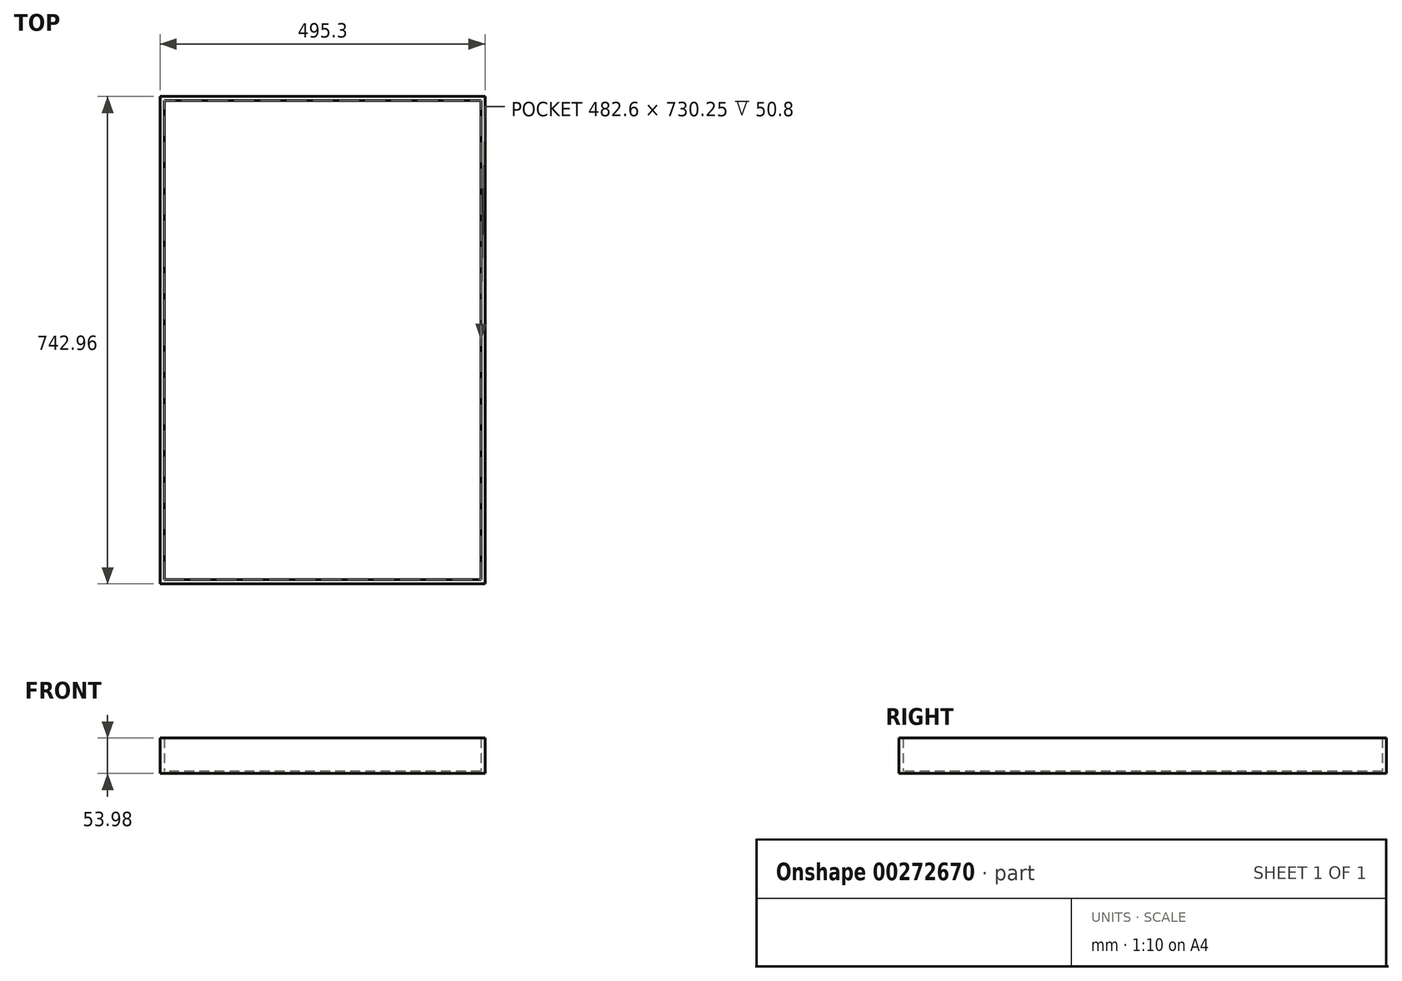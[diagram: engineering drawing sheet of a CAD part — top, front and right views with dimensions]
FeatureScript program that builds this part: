
annotation { "Feature Type Name" : "Feature", "Feature Type Description" : "" }
export const myFeature = defineFeature(function(context is Context, id is Id, definition is map)
    precondition{}
    {
        {
            var Q0;
            Q0=qCreatedBy(makeId("Top.planeOp"),FACE);
            var sketch = newSketch(context, id + "F0", { "sketchPlane" : qUnion([Q0])});
            skLineSegment(sketch, "E0.bottom", {"start": v(196.85, -320.67) * mm, "end": v(-196.85, -320.68) * mm, "construction": true});
            skLineSegment(sketch, "E0.top", {"start": v(196.85, 320.68) * mm, "end": v(-196.85, 320.68) * mm, "construction": true});
            skLineSegment(sketch, "E0.left", {"start": v(196.85, -320.67) * mm, "end": v(196.85, 320.68) * mm, "construction": true});
            skLineSegment(sketch, "E0.right", {"start": v(-196.85, -320.68) * mm, "end": v(-196.85, 320.68) * mm, "construction": true});
            skPoint(sketch, "E0.middle", {"position": v(0, 0) * mm});
            skLineSegment(sketch, "E1.0", {"start": v(247.65, 371.48) * mm, "end": v(-247.65, 371.48) * mm});
            skLineSegment(sketch, "E1.1", {"start": v(247.65, -371.47) * mm, "end": v(247.65, 371.48) * mm});
            skLineSegment(sketch, "E1.2", {"start": v(247.65, -371.47) * mm, "end": v(-247.65, -371.47) * mm});
            skLineSegment(sketch, "E1.3", {"start": v(-247.65, -371.48) * mm, "end": v(-247.65, 371.48) * mm});
            skSolve(sketch);
        }
        {
            var Q0;
            Q0 = qSketchRegion(id + "F0", true);
            extrude(context, id + "F1", {"entities" : qUnion([Q0]), "depth" : 3.17 * mm});
        }
        {
            var Q0;
            Q0=makeQuery(id+"F1.opExtrude","CAP_FACE",FACE,{"disambiguationData":[OSD([sQuery(id+"F0.wireOp",EDGE,"E1.0"),sQuery(id+"F0.wireOp",EDGE,"E1.1"),sQuery(id+"F0.wireOp",EDGE,"E1.2"),sQuery(id+"F0.wireOp",EDGE,"E1.3")])],"isStart":false});
            var sketch = newSketch(context, id + "F2", { "sketchPlane" : qUnion([Q0])});
            skLineSegment(sketch, "E2.0.0", {"start": v(-247.65, 371.48) * mm, "end": v(-247.65, -371.47) * mm});
            skLineSegment(sketch, "E2.0.1", {"start": v(-247.65, -371.47) * mm, "end": v(247.65, -371.47) * mm});
            skLineSegment(sketch, "E2.0.2", {"start": v(247.65, -371.47) * mm, "end": v(247.65, 371.48) * mm});
            skLineSegment(sketch, "E2.0.3", {"start": v(247.65, 371.48) * mm, "end": v(-247.65, 371.48) * mm});
            skLineSegment(sketch, "E3.0", {"start": v(-241.3, 365.13) * mm, "end": v(-241.3, -365.13) * mm});
            skLineSegment(sketch, "E3.1", {"start": v(241.3, 365.13) * mm, "end": v(-241.3, 365.13) * mm});
            skLineSegment(sketch, "E3.2", {"start": v(241.3, -365.13) * mm, "end": v(241.3, 365.13) * mm});
            skLineSegment(sketch, "E3.3", {"start": v(-241.3, -365.13) * mm, "end": v(241.3, -365.13) * mm});
            skSolve(sketch);
        }
        {
            var Q0;
            Q0 = qSketchRegion(id + "F2", true);
            extrude(context, id + "F3", {"entities" : qUnion([Q0]), "operationType" : NewBodyOperationType.ADD, "depth" : 50.8 * mm});
        }
    });
